# Revit family: Midmark - Mobile Digital Dental Radiography System
name_source: partatom
category: Specialty Equipment
revit_build: Autodesk Revit 2017 (Build: 20190508_0315(x64)
units: mm (PartAtom-declared; Revit-internal decimal feet)

## family parameters
Always vertical = Yes
Cut with Voids When Loaded = No
Part Type = Normal
Room Calculation Point = No
Round Connector Dimension = Use Diameter
Shared = No
Work Plane-Based = No

## types (2) — shared parameters
Arms = Midmark - White
Base = Midmark - White
Closed Arm = Yes
Control Panel = Midmark - White
Depth = 3' - 0"
Description = Coordinate cable needs upon ordering
Joint Connections = Midmark - Warm Gray
Manufacturer = Midmark
Mobile Stand = Midmark - White
Width = 2' - 2 29/32"
X-Ray Head = Midmark - White

## per-type parameters (varying)
| type | Laptop and Tray | Model | Type Comments |
| Mobile Assembly | No | DCVM-G0A/H/S4 | Mobile, Handswitch, Size #2 |
| Mobile Assembly with Laptop and Tray | Yes | DCVM-G0A/H/S4/L | Mobile, Handswitch, Size #2, Laptop, Tray |

## geometry (parser evidence)
native form markers: Sweep x6
no freeform markers — native parametric forms only
